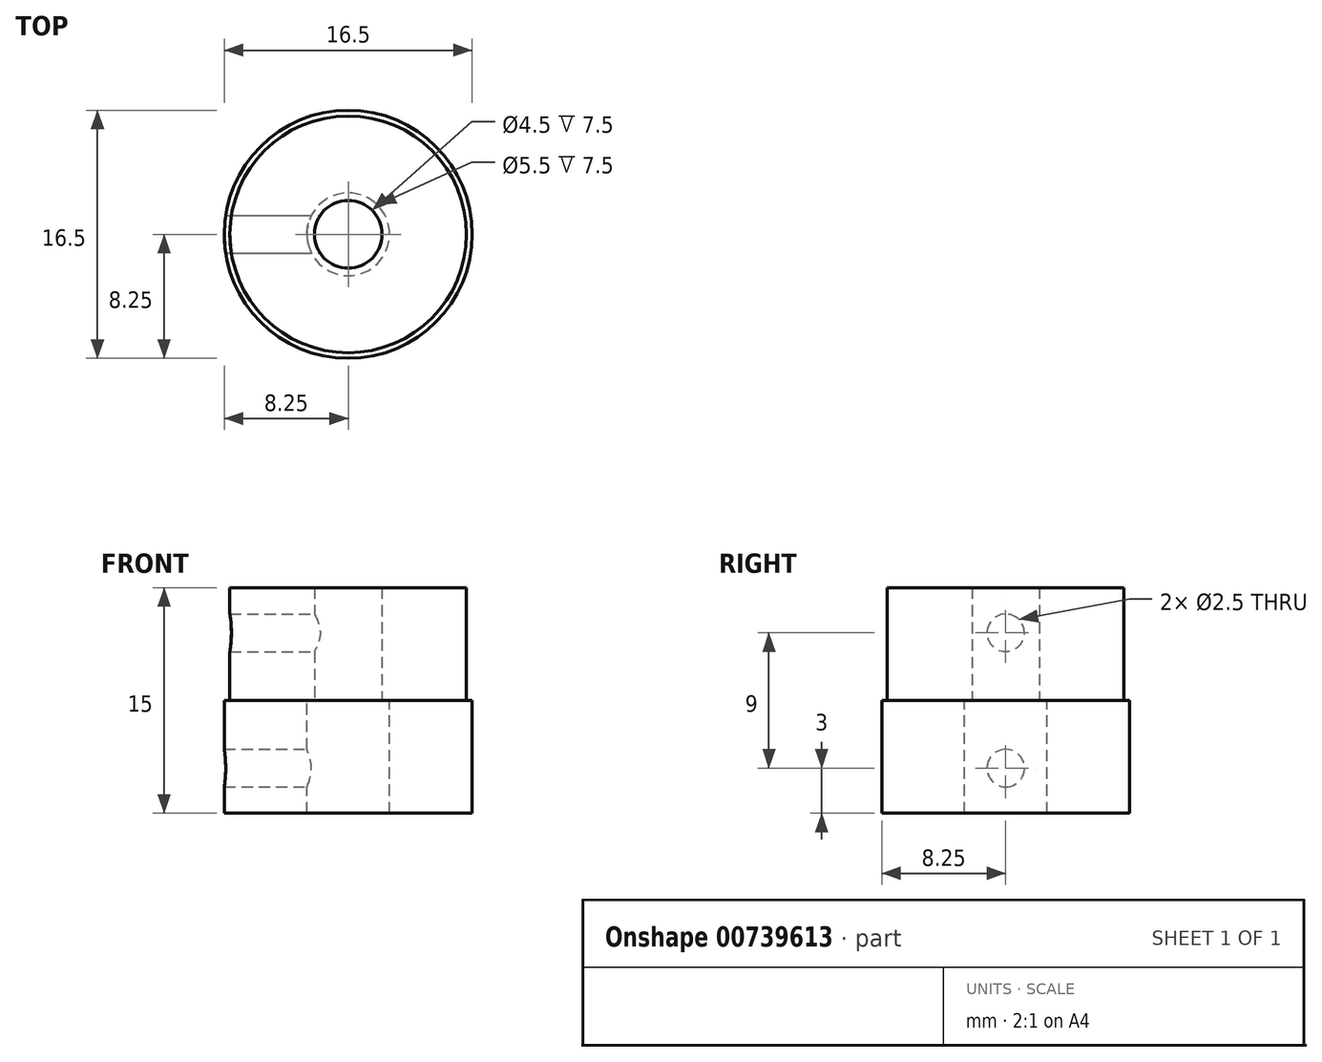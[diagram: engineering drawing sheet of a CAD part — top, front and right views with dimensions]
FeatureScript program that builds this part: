
annotation { "Feature Type Name" : "Feature", "Feature Type Description" : "" }
export const myFeature = defineFeature(function(context is Context, id is Id, definition is map)
    precondition{}
    {
        {
            var Q0;
            Q0=qCreatedBy(makeId("Top.planeOp"),FACE);
            var sketch = newSketch(context, id + "F0", { "sketchPlane" : qUnion([Q0])});
            skCircle(sketch, "E0", {"center": v(0, 0) * mm, "radius": 7.88 * mm});
            skCircle(sketch, "E1", {"center": v(0, 0) * mm, "radius": 2.25 * mm});
            skSolve(sketch);
        }
        {
            var Q0;
            Q0=qSketchRegion(id+"F0",true);
            extrude(context, id + "F1", {"entities" : qUnion([Q0]), "depth" : 7.5 * mm});
        }
        {
            var Q0;
            Q0=makeQuery(id+"F1.opExtrude","CAP_FACE",FACE,{"disambiguationData":[OSD([sQuery(id+"F0.wireOp",EDGE,"E0"),sQuery(id+"F0.wireOp",EDGE,"E1")])],"isStart":true});
            var sketch = newSketch(context, id + "F2", { "sketchPlane" : qUnion([Q0])});
            skCircle(sketch, "E2", {"center": v(0, 0) * mm, "radius": 2.75 * mm});
            skCircle(sketch, "E3", {"center": v(0, 0) * mm, "radius": 8.25 * mm});
            skSolve(sketch);
        }
        {
            var Q0;
            Q0=qSketchRegion(id+"F2",true);
            extrude(context, id + "F3", {"entities" : qUnion([Q0]), "operationType" : NewBodyOperationType.ADD, "depth" : 7.5 * mm});
        }
        {
            var Q0;
            Q0=qCreatedBy(makeId("Right.planeOp"),FACE);
            var sketch = newSketch(context, id + "F4", { "sketchPlane" : qUnion([Q0])});
            skCircle(sketch, "E4", {"center": v(0, 4.5) * mm, "radius": 1.25 * mm});
            skCircle(sketch, "E5", {"center": v(0, -4.5) * mm, "radius": 1.25 * mm});
            skSolve(sketch);
        }
        {
            var Q0;
            Q0=qSketchRegion(id+"F4",true);
            extrude(context, id + "F5", {"entities" : qUnion([Q0]), "operationType" : NewBodyOperationType.REMOVE, "oppositeDirection" : true, "depth" : 25 * mm});
        }
    });
